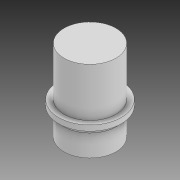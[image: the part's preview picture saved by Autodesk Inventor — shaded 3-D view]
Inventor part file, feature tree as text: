
AUTODESK INVENTOR PART (.ipt)
format: ipt  version: 2020 (Build 240168000, 168)  size: 98,816 bytes
history: native  units: mm
features: revolve x1, sketch x1
ambient origin geometry x8: Origin, YZ Plane, XZ Plane, XY Plane, X Axis, Y Axis, Z Axis, Center Point
bodies: Solid1 (feature_tree)
feature tree (2):
  revolve  "Revolution1"  [1 undecoded]
  sketch  "Sketch1"  dims[d0=2.4mm d1=2.0mm d2=1.0mm d3=4.5mm d7=45.0deg d8=0.5mm d9=90.0deg]
note: 1 required parameter value undecoded (feature->parameter linkage not recoverable at this tier; creation-order binding heuristic only, values carry confidence <= 0.55)
